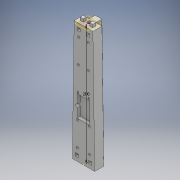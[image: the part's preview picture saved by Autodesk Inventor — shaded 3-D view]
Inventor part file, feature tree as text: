
AUTODESK INVENTOR PART (.ipt)
format: ipt  version: 2017 (Build 210142000, 142)  size: 506,368 bytes
history: native  units: mm
features: sketch x38, extrude x31, chamfer x10, loft x2, plane x1, other x1, hole x1
ambient origin geometry x8: Origin, YZ Plane, XZ Plane, XY Plane, X Axis, Y Axis, Z Axis, Center Point
bodies: Solid1 (feature_tree)
feature tree (84):
  sketch  "Sketch1"  dims[d0=37.0mm d1=15.0mm]
  sketch  "Sketch2"  dims[d2=12.5mm d3=17.0mm]
  sketch  "Sketch3"  dims[d4=10.0mm d5=200.0mm]
  plane  "Work Plane1"
  sketch  "Sketch4"  dims[d6=31.0mm d7=15.0mm]
  sketch  "Sketch5"  dims[d8=12.5mm d9=11.0mm]
  loft  "Loft1"
  loft  "Loft2"
  other  "Work Point1"
  sketch  "Sketch15"  dims[d10=10.0mm d11=0.0mm d12=90.0deg]
  sketch  "Sketch16"  dims[d13=0.0mm d14=90.0deg d15=0.0mm d16=90.0deg]
  sketch  "Sketch18"  dims[d79=0.0mm d80=2.0mm]
  sketch  "Sketch19"  dims[d81=0.0mm d82=1.2mm]
  sketch  "Sketch20"  dims[d83=1.2mm d84=6.6mm d85=0.0mm]
  extrude  "Extrusion17"  Depth=200.0mm
  extrude  "Extrusion18"  Depth=15.0mm
  extrude  "Extrusion19"  Depth=11.0mm
  extrude  "Extrusion20"  TaperAngle=0.0deg  [1 undecoded]
  extrude  "Extrusion21"  TaperAngle=0.0deg  [1 undecoded]
  extrude  "Extrusion22"  Depth=2.0mm
  extrude  "Extrusion23"  Depth=2.0mm
  extrude  "Extrusion24"  Depth=1.2mm
  extrude  "Extrusion25"  Depth=6.6mm TaperAngle=0.0deg
  extrude  "Extrusion26"  Depth=2.8mm
  extrude  "Extrusion27"  Depth=2.0mm
  extrude  "Extrusion28"  TaperAngle=0.0deg  [1 undecoded]
  extrude  "Extrusion29"  TaperAngle=0.0deg  [1 undecoded]
  extrude  "Extrusion30"  Depth=1.2mm
  extrude  "Extrusion31"  Depth=2.8mm
  extrude  "Extrusion32"  Depth=8.0mm TaperAngle=0.0deg
  extrude  "Extrusion33"  Depth=1.2mm
  extrude  "Extrusion34"  Depth=2.8mm
  extrude  "Extrusion35"  Depth=8.0mm TaperAngle=0.0deg
  extrude  "Extrusion36"  Depth=1.2mm
  chamfer  "Chamfer1"  Distance=6.6mm
  chamfer  "Chamfer2"  Distance=8.0mm
  chamfer  "Chamfer3"  Distance=6.6mm
  chamfer  "Chamfer4"  Distance=8.0mm
  chamfer  "Chamfer5"  Distance=6.6mm
  chamfer  "Chamfer6"  Distance=8.0mm
  chamfer  "Chamfer7"  Distance=6.6mm
  chamfer  "Chamfer8"  Distance=2.8mm
  chamfer  "Chamfer9"  Distance=2.8mm
  chamfer  "Chamfer10"  Distance=8.0mm
  hole  "Hole2"  [1 undecoded]
  sketch  "Sketch37"  dims[d123=2.8mm]
  sketch  "Sketch38"  dims[d124=2.8mm d125=8.0mm d126=0.0mm]
  sketch  "Sketch39"  dims[d127=2.0mm]
  sketch  "Sketch40"  dims[d128=180.0deg]
  sketch  "Sketch41"  dims[d129=1.2mm]
  extrude  "Extrusion37"  Depth=1.2mm
  extrude  "Extrusion38"  Depth=1.2mm
  extrude  "Extrusion39"  Depth=6.6mm TaperAngle=0.0deg
  extrude  "Extrusion40"  Depth=2.8mm
  extrude  "Extrusion44"  Depth=2.8mm
  extrude  "Extrusion45"  Depth=8.0mm TaperAngle=0.0deg
  extrude  "Extrusion46"  Depth=2.0mm
  sketch  "Sketch51"  dims[d137=2.0mm]
  sketch  "Sketch52"  dims[d138=180.0deg]
  sketch  "Sketch53"  dims[d139=1.2mm]
  sketch  "Sketch54"  dims[d140=1.2mm d141=6.6mm d142=0.0mm d143=2.8mm d144=2.8mm d145=8.0mm d146=0.0mm d147=2.0mm d148=1.2mm d149=1.2mm d150=6.6mm d151=0.0mm d152=2.8mm d153=2.8mm d154=8.0mm d155=0.0mm d156=2.0mm d157=180.0deg d158=1.2mm d159=1.2mm d160=6.6mm d161=0.0mm d162=2.8mm d163=2.8mm d164=8.0mm d165=0.0mm d166=2.0mm d167=180.0deg d168=1.2mm d169=1.2mm d170=6.6mm d171=0.0mm d172=2.8mm d173=2.8mm d174=8.0mm d175=0.0mm d176=0.8mm d177=2.0mm d178=45.0deg d179=0.8mm d180=2.0mm d181=45.0deg d182=0.8mm d183=2.0mm d184=45.0deg d185=0.8mm d186=2.0mm d187=45.0deg d188=0.8mm d189=2.0mm d190=45.0deg d191=0.73mm d192=2.0mm d193=45.0deg d194=0.7mm d195=2.0mm d196=45.0deg d197=0.8mm d198=2.0mm d199=45.0deg d200=0.7mm d201=2.0mm d202=45.0deg d203=0.7mm d204=2.0mm d205=45.0deg d206=15.0mm d207=6.4mm d208=6.0mm d209=4.0mm d210=2.0mm d211=90.0deg d212=8.0mm d213=20.594885mm d214=7.5mm d215=9.0mm d216=5.0mm d217=5.0mm d218=7.5mm d219=9.0mm d220=5.0mm d221=5.0mm d222=7.5mm d223=9.0mm d224=5.0mm d225=5.0mm d226=7.5mm d227=9.0mm d228=5.0mm d229=5.0mm d230=6.0mm d231=0.0mm d232=6.0mm d233=0.0mm d234=6.0mm d235=0.0mm d236=6.0mm d237=0.0mm d249=5.5mm d250=5.5mm d251=6.0mm d252=0.0mm d253=21.0mm d254=35.0mm d255=5.0mm d256=0.0mm d257=5.0mm d258=5.0mm d259=0.0mm d264=5.0mm d265=5.0mm d266=5.0mm d267=5.0mm d268=5.0mm d269=5.0mm d270=5.0mm d271=5.0mm d280=4.75mm d281=4.75mm d282=5.5mm d283=5.5mm d284=4.75mm d285=4.75mm d286=5.5mm d287=5.5mm d288=6.0mm d289=0.0mm d290=6.0mm d291=0.0mm d292=5.0mm d293=0.0mm d294=5.0mm d295=0.0mm]
  extrude  "Extrusion51"  TaperAngle=180.0deg  [1 undecoded]
  extrude  "Extrusion52"  Depth=1.2mm
  extrude  "Extrusion53"  Depth=1.2mm
  extrude  "Extrusion54"  Depth=6.6mm TaperAngle=0.0deg
  sketch  "Sketch17"  dims[d17=0.0mm d18=90.0deg d78=2.0mm]
  sketch  "Sketch21"  dims[d86=2.8mm d87=2.8mm]
  sketch  "Sketch22"  dims[d88=8.0mm d89=0.0mm d90=2.0mm]
  sketch  "Sketch23"  dims[d91=2.0mm d92=0.0mm]
  sketch  "Sketch24"  dims[d93=2.0mm d94=0.0mm]
  sketch  "Sketch26"  dims[d95=1.2mm d96=1.2mm]
  sketch  "Sketch27"  dims[d97=6.6mm d98=0.0mm d99=2.8mm]
  sketch  "Sketch28"  dims[d100=2.8mm d101=8.0mm d102=0.0mm]
  sketch  "Sketch29"  dims[d103=1.2mm d104=1.2mm]
  sketch  "Sketch30"  dims[d105=6.6mm d106=0.0mm d107=2.8mm]
  sketch  "Sketch31"  dims[d108=2.8mm d109=8.0mm d110=0.0mm]
  sketch  "Sketch32"  dims[d111=1.2mm d112=1.2mm d113=6.6mm d114=0.0mm]
  sketch  "Sketch33"  dims[d115=2.8mm]
  sketch  "Sketch34"  dims[d116=2.8mm d117=8.0mm d118=0.0mm]
  sketch  "Sketch35"  dims[d119=1.2mm]
  sketch  "Sketch36"  dims[d120=1.2mm d121=6.6mm d122=0.0mm]
  sketch  "Sketch46"  dims[d130=1.2mm d131=6.6mm d132=0.0mm]
  sketch  "Sketch47"  dims[d133=2.8mm]
  sketch  "Sketch48"  dims[d134=2.8mm d135=8.0mm d136=0.0mm]
note: 6 required parameter values undecoded (feature->parameter linkage not recoverable at this tier; creation-order binding heuristic only, values carry confidence <= 0.55)
